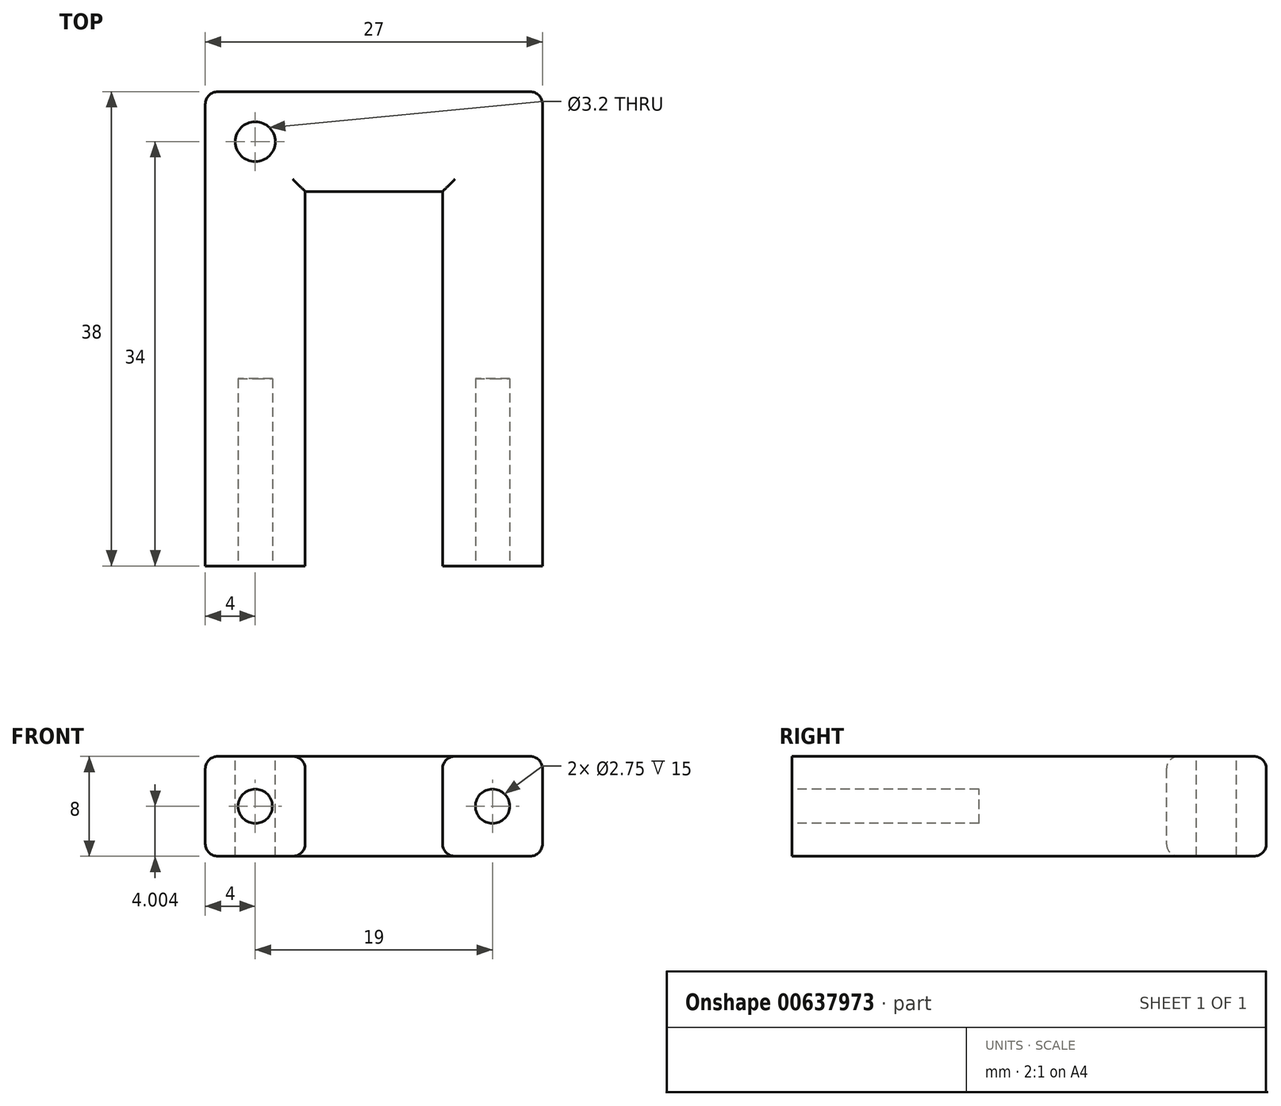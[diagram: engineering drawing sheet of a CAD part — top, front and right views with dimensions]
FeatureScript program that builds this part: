
annotation { "Feature Type Name" : "Feature", "Feature Type Description" : "" }
export const myFeature = defineFeature(function(context is Context, id is Id, definition is map)
    precondition{}
    {
        {
            var Q0;
            Q0=qCreatedBy(makeId("Front.planeOp"),FACE);
            var sketch = newSketch(context, id + "F0", { "sketchPlane" : qUnion([Q0])});
            skLineSegment(sketch, "E0.bottom", {"start": v(-44.5, 25.07) * mm, "end": v(-36.5, 25.07) * mm});
            skLineSegment(sketch, "E0.top", {"start": v(-44.5, 17.07) * mm, "end": v(-36.5, 17.07) * mm});
            skLineSegment(sketch, "E0.left", {"start": v(-44.5, 25.07) * mm, "end": v(-44.5, 17.07) * mm});
            skLineSegment(sketch, "E0.right", {"start": v(-36.5, 25.07) * mm, "end": v(-36.5, 17.07) * mm});
            skLineSegment(sketch, "E1", {"start": v(-44.5, 17.07) * mm, "end": v(50.5, 17.07) * mm, "construction": true});
            skPoint(sketch, "E1.endSnap0", {"position": v(-40.5, 17.07) * mm});
            skLineSegment(sketch, "E2.bottom", {"start": v(-25.5, 17.07) * mm, "end": v(-17.5, 17.07) * mm});
            skLineSegment(sketch, "E2.top", {"start": v(-25.5, 25.07) * mm, "end": v(-17.5, 25.07) * mm});
            skLineSegment(sketch, "E2.left", {"start": v(-25.5, 17.07) * mm, "end": v(-25.5, 25.07) * mm});
            skLineSegment(sketch, "E2.right", {"start": v(-17.5, 17.07) * mm, "end": v(-17.5, 25.07) * mm});
            skSolve(sketch);
        }
        {
            var Q0;
            Q0=makeQuery(id+"F0.imprint","IMPRINT",FACE,{"disambiguationData":[TD([[makeQuery(id+"F0.imprint","IMPRINT",EDGE,{"derivedFrom":sQuery(id+"F0.wireOp",EDGE,"E0.bottom")}),-1.0]])]});
            var Q1;
            Q1=makeQuery(id+"F0.imprint","IMPRINT",FACE,{"disambiguationData":[TD([[makeQuery(id+"F0.imprint","IMPRINT",EDGE,{"derivedFrom":sQuery(id+"F0.wireOp",EDGE,"E2.bottom")}),1.0]])]});
            extrude(context, id + "F1", {"entities" : qUnion([Q0, Q1]), "depth" : 30 * mm, "offsetDistance" : 25 * mm});
        }
        {
            var Q0;
            Q0=qCreatedBy(makeId("Front.planeOp"),FACE);
            var sketch = newSketch(context, id + "F2", { "sketchPlane" : qUnion([Q0])});
            skLineSegment(sketch, "E3.0.0", {"start": v(-25.5, 25.07) * mm, "end": v(-17.5, 25.07) * mm});
            skLineSegment(sketch, "E3.0.1", {"start": v(-17.5, 25.07) * mm, "end": v(-17.5, 17.07) * mm});
            skLineSegment(sketch, "E3.0.2", {"start": v(-17.5, 17.07) * mm, "end": v(-25.5, 17.07) * mm});
            skLineSegment(sketch, "E4.0.0", {"start": v(-44.5, 17.07) * mm, "end": v(-44.5, 25.07) * mm});
            skLineSegment(sketch, "E4.0.1", {"start": v(-44.5, 25.07) * mm, "end": v(-36.5, 25.07) * mm});
            skLineSegment(sketch, "E4.0.3", {"start": v(-36.5, 17.07) * mm, "end": v(-44.5, 17.07) * mm});
            skLineSegment(sketch, "E5.bottom", {"start": v(-17.5, 25.07) * mm, "end": v(-44.5, 25.07) * mm});
            skLineSegment(sketch, "E5.top", {"start": v(-17.5, 17.07) * mm, "end": v(-44.5, 17.07) * mm});
            skLineSegment(sketch, "E5.right", {"start": v(-44.5, 25.07) * mm, "end": v(-44.5, 17.07) * mm});
            skSolve(sketch);
        }
        {
            var Q0;
            {var subQ0=sQuery(id+"F2.wireOp",EDGE,"E3.0.1");Q0=makeQuery(id+"F2.imprint","IMPRINT",FACE,{"disambiguationData":[TD([[makeQuery(id+"F2.imprint","IMPRINT",EDGE,{"derivedFrom":subQ0}),-1.0]])]});}
            extrude(context, id + "F3", {"entities" : qUnion([Q0]), "oppositeDirection" : true, "depth" : 8 * mm, "offsetDistance" : 25 * mm});
        }
        {
            var Q0;
            Q0=makeQuery(id+"F3.opExtrude","SWEPT_FACE",FACE,{"disambiguationData":[OSD([sQuery(id+"F2.wireOp",EDGE,"E5.bottom")])]});
            var sketch = newSketch(context, id + "F4", { "sketchPlane" : qUnion([Q0])});
            skLineSegment(sketch, "E6.0", {"start": v(-36.5, -30) * mm, "end": v(-36.5, 0) * mm});
            skLineSegment(sketch, "E7.0", {"start": v(-17.5, 0) * mm, "end": v(-44.5, 0) * mm});
            skLineSegment(sketch, "E8.0", {"start": v(-44.5, 8) * mm, "end": v(-44.5, 0) * mm});
            skLineSegment(sketch, "E9.0", {"start": v(-17.5, 8) * mm, "end": v(-44.5, 8) * mm});
            skCircle(sketch, "E10", {"center": v(-40.5, 4) * mm, "radius": 1.6 * mm});
            skSolve(sketch);
        }
        {
            var Q0;
            Q0=makeQuery(id+"F4.imprint","IMPRINT",FACE,{"disambiguationData":[TD([[makeQuery(id+"F4.imprint","IMPRINT",EDGE,{"derivedFrom":sQuery(id+"F4.wireOp",EDGE,"E10")}),1.0]])]});
            extrude(context, id + "F5", {"entities" : qUnion([Q0]), "operationType" : NewBodyOperationType.REMOVE, "endBound" : BoundingType.UP_TO_NEXT, "oppositeDirection" : true, "depth" : 25 * mm, "offsetDistance" : 25 * mm});
        }
        {
            var Q0;
            Q0=makeQuery(id+"F1.opExtrude","SWEPT_BODY",BODY,{"disambiguationData":[OSD([sQuery(id+"F0.wireOp",EDGE,"E0.bottom"),sQuery(id+"F0.wireOp",EDGE,"E0.top"),sQuery(id+"F0.wireOp",EDGE,"E0.left"),sQuery(id+"F0.wireOp",EDGE,"E0.right")])]});
            var Q1;
            Q1=makeQuery(id+"F3.opExtrude","SWEPT_BODY",BODY,{"disambiguationData":[OSD([sQuery(id+"F2.wireOp",EDGE,"E5.bottom"),sQuery(id+"F2.wireOp",EDGE,"E5.top"),sQuery(id+"F2.wireOp",EDGE,"E3.0.1"),sQuery(id+"F2.wireOp",EDGE,"E5.right")])]});
            var Q2;
            Q2=makeQuery(id+"F1.opExtrude","SWEPT_BODY",BODY,{"disambiguationData":[OSD([sQuery(id+"F0.wireOp",EDGE,"E2.bottom"),sQuery(id+"F0.wireOp",EDGE,"E2.top"),sQuery(id+"F0.wireOp",EDGE,"E2.left"),sQuery(id+"F0.wireOp",EDGE,"E2.right")])]});
            booleanBodies(context, id + "F6", {"operationType" : BooleanOperationType.UNION, "tools" : qUnion([Q0, Q1, Q2])});
        }
        {
            var Q0;
            Q0=makeQuery(id+"F1.opExtrude","CAP_FACE",FACE,{"disambiguationData":[OSD([sQuery(id+"F0.wireOp",EDGE,"E0.bottom"),sQuery(id+"F0.wireOp",EDGE,"E0.top"),sQuery(id+"F0.wireOp",EDGE,"E0.left"),sQuery(id+"F0.wireOp",EDGE,"E0.right")])],"isStart":false});
            var sketch = newSketch(context, id + "F7", { "sketchPlane" : qUnion([Q0])});
            skLineSegment(sketch, "E11.0", {"start": v(-44.5, 25.07) * mm, "end": v(-44.5, 17.07) * mm});
            skLineSegment(sketch, "E12.0", {"start": v(-36.5, 25.07) * mm, "end": v(-36.5, 17.07) * mm});
            skCircle(sketch, "E13", {"center": v(-40.5, 21.07) * mm, "radius": 1.38 * mm});
            skCircle(sketch, "E14", {"center": v(-21.5, 21.07) * mm, "radius": 1.38 * mm});
            skSolve(sketch);
        }
        {
            var Q0;
            Q0=makeQuery(id+"F7.imprint","IMPRINT",FACE,{"disambiguationData":[TD([[makeQuery(id+"F7.imprint","IMPRINT",EDGE,{"derivedFrom":sQuery(id+"F7.wireOp",EDGE,"E13")}),1.0]])]});
            var Q1;
            Q1=makeQuery(id+"F7.imprint","IMPRINT",FACE,{"disambiguationData":[TD([[makeQuery(id+"F7.imprint","IMPRINT",EDGE,{"derivedFrom":sQuery(id+"F7.wireOp",EDGE,"E14")}),1.0]])]});
            extrude(context, id + "F8", {"entities" : qUnion([Q0, Q1]), "operationType" : NewBodyOperationType.REMOVE, "oppositeDirection" : true, "depth" : 15 * mm, "offsetDistance" : 25 * mm});
        }
        {
            var Q0;
            Q0=makeQuery(id+"F6.opBoolean","MERGE",EDGE,{"derivedFrom":[makeQuery(id+"F1.opExtrude","SWEPT_EDGE",EDGE,{"disambiguationData":[OSD([sQuery(id+"F0.wireOp",EDGE,"E0.bottom"),sQuery(id+"F0.wireOp",EDGE,"E0.left")])]}),makeQuery(id+"F3.opExtrude","SWEPT_EDGE",EDGE,{"disambiguationData":[OSD([sQuery(id+"F2.wireOp",EDGE,"E5.bottom"),sQuery(id+"F2.wireOp",EDGE,"E5.right")])]})]});
            var Q1;
            Q1=makeQuery(id+"F1.opExtrude","SWEPT_EDGE",EDGE,{"disambiguationData":[OSD([sQuery(id+"F0.wireOp",EDGE,"E0.bottom"),sQuery(id+"F0.wireOp",EDGE,"E0.right")])]});
            var Q2;
            Q2=makeQuery(id+"F3.opExtrude","CAP_EDGE",EDGE,{"disambiguationData":[OSD([sQuery(id+"F2.wireOp",EDGE,"E5.bottom")])],"isStart":true});
            var Q3;
            Q3=makeQuery(id+"F3.opExtrude","CAP_FACE",FACE,{"disambiguationData":[OSD([sQuery(id+"F2.wireOp",EDGE,"E5.bottom"),sQuery(id+"F2.wireOp",EDGE,"E5.top"),sQuery(id+"F2.wireOp",EDGE,"E3.0.1"),sQuery(id+"F2.wireOp",EDGE,"E5.right")])],"isStart":false});
            var Q4;
            Q4=makeQuery(id+"F1.opExtrude","SWEPT_EDGE",EDGE,{"disambiguationData":[OSD([sQuery(id+"F0.wireOp",EDGE,"E2.top"),sQuery(id+"F0.wireOp",EDGE,"E2.left")])]});
            var Q5;
            Q5=makeQuery(id+"F6.opBoolean","MERGE",EDGE,{"derivedFrom":[makeQuery(id+"F1.opExtrude","SWEPT_EDGE",EDGE,{"disambiguationData":[OSD([sQuery(id+"F0.wireOp",EDGE,"E2.top"),sQuery(id+"F0.wireOp",EDGE,"E2.right")])]}),makeQuery(id+"F3.opExtrude","SWEPT_EDGE",EDGE,{"disambiguationData":[OSD([sQuery(id+"F2.wireOp",EDGE,"E5.bottom"),sQuery(id+"F2.wireOp",EDGE,"E3.0.1")])]})]});
            var Q6;
            Q6=makeQuery(id+"F6.opBoolean","MERGE",EDGE,{"derivedFrom":[makeQuery(id+"F1.opExtrude","SWEPT_EDGE",EDGE,{"disambiguationData":[OSD([sQuery(id+"F0.wireOp",EDGE,"E2.bottom"),sQuery(id+"F0.wireOp",EDGE,"E2.right")])]}),makeQuery(id+"F3.opExtrude","SWEPT_EDGE",EDGE,{"disambiguationData":[OSD([sQuery(id+"F2.wireOp",EDGE,"E5.top"),sQuery(id+"F2.wireOp",EDGE,"E3.0.1")])]})]});
            var Q7;
            Q7=makeQuery(id+"F1.opExtrude","SWEPT_EDGE",EDGE,{"disambiguationData":[OSD([sQuery(id+"F0.wireOp",EDGE,"E2.bottom"),sQuery(id+"F0.wireOp",EDGE,"E2.left")])]});
            var Q8;
            Q8=makeQuery(id+"F3.opExtrude","CAP_EDGE",EDGE,{"disambiguationData":[OSD([sQuery(id+"F2.wireOp",EDGE,"E5.top")])],"isStart":true});
            var Q9;
            Q9=makeQuery(id+"F1.opExtrude","SWEPT_EDGE",EDGE,{"disambiguationData":[OSD([sQuery(id+"F0.wireOp",EDGE,"E0.top"),sQuery(id+"F0.wireOp",EDGE,"E0.right")])]});
            var Q10;
            Q10=makeQuery(id+"F6.opBoolean","MERGE",EDGE,{"derivedFrom":[makeQuery(id+"F1.opExtrude","SWEPT_EDGE",EDGE,{"disambiguationData":[OSD([sQuery(id+"F0.wireOp",EDGE,"E0.top"),sQuery(id+"F0.wireOp",EDGE,"E0.left")])]}),makeQuery(id+"F3.opExtrude","SWEPT_EDGE",EDGE,{"disambiguationData":[OSD([sQuery(id+"F2.wireOp",EDGE,"E5.top"),sQuery(id+"F2.wireOp",EDGE,"E5.right")])]})]});
            fillet(context, id + "F9", {"entities" : qUnion([Q0, Q1, Q2, Q3, Q4, Q5, Q6, Q7, Q8, Q9, Q10]), "radius" : 1 * mm, "tangentPropagation" : true, "allowEdgeOverflow" : false});
        }
    });
